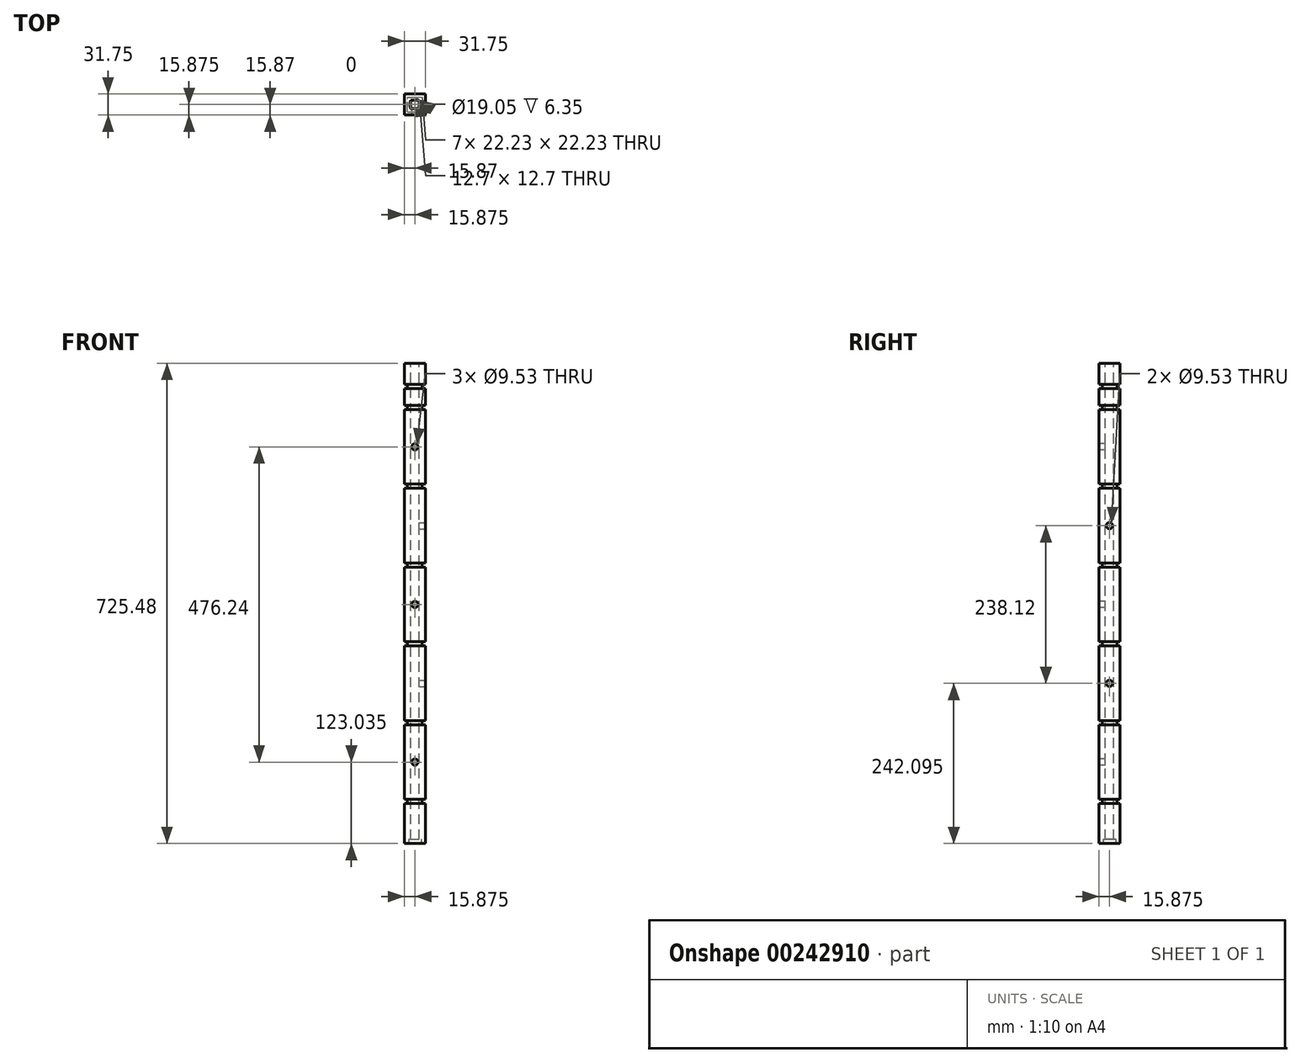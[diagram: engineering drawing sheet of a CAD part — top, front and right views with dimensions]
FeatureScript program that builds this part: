
annotation { "Feature Type Name" : "Feature", "Feature Type Description" : "" }
export const myFeature = defineFeature(function(context is Context, id is Id, definition is map)
    precondition{}
    {
        {
            var Q0;
            Q0=qCreatedBy(makeId("Top.planeOp"),FACE);
            var sketch = newSketch(context, id + "F0", { "sketchPlane" : qUnion([Q0])});
            skLineSegment(sketch, "E0", {"start": v(0, 0) * mm, "end": v(0, 31.75) * mm});
            skLineSegment(sketch, "E1", {"start": v(0, 31.75) * mm, "end": v(31.75, 31.75) * mm});
            skLineSegment(sketch, "E2", {"start": v(31.75, 31.75) * mm, "end": v(31.75, 0) * mm});
            skLineSegment(sketch, "E3", {"start": v(31.75, 0) * mm, "end": v(0, 0) * mm});
            skSolve(sketch);
        }
        {
            var Q0;
            Q0=makeQuery(id+"F0.imprint","IMPRINT",FACE,{"disambiguationData":[TD([[makeQuery(id+"F0.imprint","IMPRINT",EDGE,{"derivedFrom":sQuery(id+"F0.wireOp",EDGE,"E0")}),-1.0]])]});
            extrude(context, id + "F1", {"entities" : qUnion([Q0]), "depth" : 60.33 * mm});
        }
        {
            var Q0;
            Q0=makeQuery(id+"F1.opExtrude","CAP_FACE",FACE,{"disambiguationData":[OSD([sQuery(id+"F0.wireOp",EDGE,"E0"),sQuery(id+"F0.wireOp",EDGE,"E1"),sQuery(id+"F0.wireOp",EDGE,"E2"),sQuery(id+"F0.wireOp",EDGE,"E3")])],"isStart":false});
            var sketch = newSketch(context, id + "F2", { "sketchPlane" : qUnion([Q0])});
            skLineSegment(sketch, "E4", {"start": v(4.76, 4.76) * mm, "end": v(4.76, 26.99) * mm});
            skLineSegment(sketch, "E5", {"start": v(4.76, 26.99) * mm, "end": v(26.99, 26.99) * mm});
            skLineSegment(sketch, "E6", {"start": v(26.99, 26.99) * mm, "end": v(26.99, 4.76) * mm});
            skLineSegment(sketch, "E7", {"start": v(26.99, 4.76) * mm, "end": v(4.76, 4.76) * mm});
            skSolve(sketch);
        }
        {
            var Q0;
            Q0=makeQuery(id+"F2.imprint","IMPRINT",FACE,{"disambiguationData":[TD([[makeQuery(id+"F2.imprint","IMPRINT",EDGE,{"derivedFrom":sQuery(id+"F2.wireOp",EDGE,"E4")}),-1.0]])]});
            extrude(context, id + "F3", {"entities" : qUnion([Q0]), "operationType" : NewBodyOperationType.ADD, "depth" : 6.35 * mm});
        }
        {
            var Q0;
            Q0=makeQuery(id+"F3.opExtrude","CAP_FACE",FACE,{"disambiguationData":[OSD([sQuery(id+"F2.wireOp",EDGE,"E4"),sQuery(id+"F2.wireOp",EDGE,"E5"),sQuery(id+"F2.wireOp",EDGE,"E6"),sQuery(id+"F2.wireOp",EDGE,"E7")])],"isStart":false});
            var sketch = newSketch(context, id + "F4", { "sketchPlane" : qUnion([Q0])});
            skLineSegment(sketch, "E8.bottom", {"start": v(0, 0) * mm, "end": v(31.75, 0) * mm});
            skLineSegment(sketch, "E8.top", {"start": v(0, 31.75) * mm, "end": v(31.75, 31.75) * mm});
            skLineSegment(sketch, "E8.left", {"start": v(0, 0) * mm, "end": v(0, 31.75) * mm});
            skLineSegment(sketch, "E8.right", {"start": v(31.75, 0) * mm, "end": v(31.75, 31.75) * mm});
            skSolve(sketch);
        }
        {
            var Q0;
            Q0 = qSketchRegion(id + "F4", true);
            extrude(context, id + "F5", {"entities" : qUnion([Q0]), "operationType" : NewBodyOperationType.ADD, "depth" : 112.7 * mm});
        }
        {
            var Q0;
            Q0=makeQuery(id+"F5.opExtrude","CAP_FACE",FACE,{"disambiguationData":[OSD([sQuery(id+"F4.wireOp",EDGE,"E8.bottom"),sQuery(id+"F4.wireOp",EDGE,"E8.top"),sQuery(id+"F4.wireOp",EDGE,"E8.left"),sQuery(id+"F4.wireOp",EDGE,"E8.right")])],"isStart":false});
            var sketch = newSketch(context, id + "F6", { "sketchPlane" : qUnion([Q0])});
            skLineSegment(sketch, "E9.bottom", {"start": v(0, 0) * mm, "end": v(4.76, 0) * mm});
            skLineSegment(sketch, "E9.top", {"start": v(0, 4.76) * mm, "end": v(4.76, 4.76) * mm});
            skLineSegment(sketch, "E9.left", {"start": v(0, 0) * mm, "end": v(0, 4.76) * mm});
            skLineSegment(sketch, "E9.right", {"start": v(4.76, 0) * mm, "end": v(4.76, 4.76) * mm});
            skLineSegment(sketch, "E10.bottom", {"start": v(4.76, 4.76) * mm, "end": v(26.99, 4.76) * mm});
            skLineSegment(sketch, "E10.top", {"start": v(4.76, 26.99) * mm, "end": v(26.99, 26.99) * mm});
            skLineSegment(sketch, "E10.left", {"start": v(4.76, 4.76) * mm, "end": v(4.76, 26.99) * mm});
            skLineSegment(sketch, "E10.right", {"start": v(26.99, 4.76) * mm, "end": v(26.99, 26.99) * mm});
            skSolve(sketch);
        }
        {
            var Q0;
            Q0=makeQuery(id+"F6.imprint","IMPRINT",FACE,{"disambiguationData":[TD([[makeQuery(id+"F6.imprint","IMPRINT",EDGE,{"derivedFrom":sQuery(id+"F6.wireOp",EDGE,"E10.bottom")}),1.0]])]});
            extrude(context, id + "F7", {"entities" : qUnion([Q0]), "operationType" : NewBodyOperationType.ADD, "depth" : 6.35 * mm});
        }
        {
            var Q0;
            Q0=makeQuery(id+"F7.opExtrude","CAP_FACE",FACE,{"disambiguationData":[OSD([sQuery(id+"F6.wireOp",EDGE,"E10.bottom"),sQuery(id+"F6.wireOp",EDGE,"E10.top"),sQuery(id+"F6.wireOp",EDGE,"E10.left"),sQuery(id+"F6.wireOp",EDGE,"E10.right")])],"isStart":false});
            var sketch = newSketch(context, id + "F8", { "sketchPlane" : qUnion([Q0])});
            skLineSegment(sketch, "E11.bottom", {"start": v(0, 0) * mm, "end": v(31.75, 0) * mm});
            skLineSegment(sketch, "E11.top", {"start": v(0, 31.75) * mm, "end": v(31.75, 31.75) * mm});
            skLineSegment(sketch, "E11.left", {"start": v(0, 0) * mm, "end": v(0, 31.75) * mm});
            skLineSegment(sketch, "E11.right", {"start": v(31.75, 0) * mm, "end": v(31.75, 31.75) * mm});
            skSolve(sketch);
        }
        {
            var Q0;
            Q0=makeQuery(id+"F8.imprint","IMPRINT",FACE,{"disambiguationData":[TD([[makeQuery(id+"F8.imprint","IMPRINT",EDGE,{"derivedFrom":sQuery(id+"F8.wireOp",EDGE,"E11.bottom")}),1.0]])]});
            var Q1;
            Q1=makeQuery(id+"F8.imprint","IMPRINT",FACE,{"disambiguationData":[TD([[makeQuery(id+"F8.imprint","IMPRINT",EDGE,{"derivedFrom":makeQuery(id+"F7.opExtrude","CAP_EDGE",EDGE,{"disambiguationData":[OSD([sQuery(id+"F6.wireOp",EDGE,"E10.bottom")])],"isStart":false})}),1.0]])]});
            extrude(context, id + "F9", {"entities" : qUnion([Q0, Q1]), "operationType" : NewBodyOperationType.ADD, "depth" : 112.7 * mm});
        }
        {
            var Q0;
            Q0=makeQuery(id+"F9.opExtrude","CAP_FACE",FACE,{"disambiguationData":[OSD([sQuery(id+"F8.wireOp",EDGE,"E11.bottom"),sQuery(id+"F8.wireOp",EDGE,"E11.top"),sQuery(id+"F8.wireOp",EDGE,"E11.left"),sQuery(id+"F8.wireOp",EDGE,"E11.right")])],"isStart":false});
            var sketch = newSketch(context, id + "F10", { "sketchPlane" : qUnion([Q0])});
            skLineSegment(sketch, "E12.bottom", {"start": v(0, 0) * mm, "end": v(4.76, 0) * mm});
            skLineSegment(sketch, "E12.top", {"start": v(0, 4.76) * mm, "end": v(4.76, 4.76) * mm});
            skLineSegment(sketch, "E12.left", {"start": v(0, 0) * mm, "end": v(0, 4.76) * mm});
            skLineSegment(sketch, "E12.right", {"start": v(4.76, 0) * mm, "end": v(4.76, 4.76) * mm});
            skLineSegment(sketch, "E13.bottom", {"start": v(4.76, 4.76) * mm, "end": v(27, 4.76) * mm});
            skLineSegment(sketch, "E13.top", {"start": v(4.76, 26.99) * mm, "end": v(26.99, 26.99) * mm});
            skLineSegment(sketch, "E13.left", {"start": v(4.76, 4.76) * mm, "end": v(4.76, 26.99) * mm});
            skLineSegment(sketch, "E13.right", {"start": v(27, 4.76) * mm, "end": v(26.99, 26.99) * mm});
            skLineSegment(sketch, "E14.bottom", {"start": v(26.99, 26.99) * mm, "end": v(31.75, 26.99) * mm});
            skLineSegment(sketch, "E14.top", {"start": v(26.99, 31.75) * mm, "end": v(31.75, 31.75) * mm});
            skLineSegment(sketch, "E14.left", {"start": v(26.99, 26.99) * mm, "end": v(26.99, 31.75) * mm});
            skLineSegment(sketch, "E14.right", {"start": v(31.75, 26.99) * mm, "end": v(31.75, 31.75) * mm});
            skSolve(sketch);
        }
        {
            var Q0;
            Q0=makeQuery(id+"F10.imprint","IMPRINT",FACE,{"disambiguationData":[TD([[makeQuery(id+"F10.imprint","IMPRINT",EDGE,{"derivedFrom":sQuery(id+"F10.wireOp",EDGE,"E13.bottom")}),1.0]])]});
            extrude(context, id + "F11", {"entities" : qUnion([Q0]), "operationType" : NewBodyOperationType.ADD, "depth" : 6.35 * mm});
        }
        {
            var Q0;
            Q0=makeQuery(id+"F11.opExtrude","CAP_FACE",FACE,{"disambiguationData":[OSD([sQuery(id+"F10.wireOp",EDGE,"E13.bottom"),sQuery(id+"F10.wireOp",EDGE,"E13.top"),sQuery(id+"F10.wireOp",EDGE,"E13.left"),sQuery(id+"F10.wireOp",EDGE,"E13.right")])],"isStart":false});
            var sketch = newSketch(context, id + "F12", { "sketchPlane" : qUnion([Q0])});
            skLineSegment(sketch, "E15.bottom", {"start": v(0, 0) * mm, "end": v(31.75, 0) * mm});
            skLineSegment(sketch, "E15.top", {"start": v(0, 31.75) * mm, "end": v(31.75, 31.75) * mm});
            skLineSegment(sketch, "E15.left", {"start": v(0, 0) * mm, "end": v(0, 31.75) * mm});
            skLineSegment(sketch, "E15.right", {"start": v(31.75, 0) * mm, "end": v(31.75, 31.75) * mm});
            skSolve(sketch);
        }
        {
            var Q0;
            Q0=makeQuery(id+"F12.imprint","IMPRINT",FACE,{"disambiguationData":[TD([[makeQuery(id+"F12.imprint","IMPRINT",EDGE,{"derivedFrom":makeQuery(id+"F11.opExtrude","CAP_EDGE",EDGE,{"disambiguationData":[OSD([sQuery(id+"F10.wireOp",EDGE,"E13.bottom")])],"isStart":false})}),1.0]])]});
            var Q1;
            Q1=makeQuery(id+"F12.imprint","IMPRINT",FACE,{"disambiguationData":[TD([[makeQuery(id+"F12.imprint","IMPRINT",EDGE,{"derivedFrom":sQuery(id+"F12.wireOp",EDGE,"E15.bottom")}),1.0]])]});
            extrude(context, id + "F13", {"entities" : qUnion([Q0, Q1]), "operationType" : NewBodyOperationType.ADD, "depth" : 112.7 * mm});
        }
        {
            var Q0;
            Q0=makeQuery(id+"F13.opExtrude","CAP_FACE",FACE,{"disambiguationData":[OSD([sQuery(id+"F12.wireOp",EDGE,"E15.bottom"),sQuery(id+"F12.wireOp",EDGE,"E15.top"),sQuery(id+"F12.wireOp",EDGE,"E15.left"),sQuery(id+"F12.wireOp",EDGE,"E15.right")])],"isStart":false});
            var sketch = newSketch(context, id + "F14", { "sketchPlane" : qUnion([Q0])});
            skLineSegment(sketch, "E16.bottom", {"start": v(0, 0) * mm, "end": v(4.76, 0) * mm});
            skLineSegment(sketch, "E16.top", {"start": v(0, 4.76) * mm, "end": v(4.76, 4.76) * mm});
            skLineSegment(sketch, "E16.left", {"start": v(0, 0) * mm, "end": v(0, 4.76) * mm});
            skLineSegment(sketch, "E16.right", {"start": v(4.76, 0) * mm, "end": v(4.76, 4.76) * mm});
            skLineSegment(sketch, "E17.bottom", {"start": v(4.76, 4.76) * mm, "end": v(27, 4.76) * mm});
            skLineSegment(sketch, "E17.top", {"start": v(4.76, 26.99) * mm, "end": v(26.99, 26.99) * mm});
            skLineSegment(sketch, "E17.left", {"start": v(4.76, 4.76) * mm, "end": v(4.76, 26.99) * mm});
            skLineSegment(sketch, "E17.right", {"start": v(27, 4.76) * mm, "end": v(26.99, 26.99) * mm});
            skLineSegment(sketch, "E18.bottom", {"start": v(26.99, 26.99) * mm, "end": v(31.75, 26.99) * mm});
            skLineSegment(sketch, "E18.top", {"start": v(26.99, 31.75) * mm, "end": v(31.75, 31.75) * mm});
            skLineSegment(sketch, "E18.left", {"start": v(26.99, 26.99) * mm, "end": v(26.99, 31.75) * mm});
            skLineSegment(sketch, "E18.right", {"start": v(31.75, 26.99) * mm, "end": v(31.75, 31.75) * mm});
            skSolve(sketch);
        }
        {
            var Q0;
            Q0=makeQuery(id+"F14.imprint","IMPRINT",FACE,{"disambiguationData":[TD([[makeQuery(id+"F14.imprint","IMPRINT",EDGE,{"derivedFrom":sQuery(id+"F14.wireOp",EDGE,"E17.bottom")}),1.0]])]});
            extrude(context, id + "F15", {"entities" : qUnion([Q0]), "operationType" : NewBodyOperationType.ADD, "depth" : 6.35 * mm});
        }
        {
            var Q0;
            Q0=makeQuery(id+"F15.opExtrude","CAP_FACE",FACE,{"disambiguationData":[OSD([sQuery(id+"F14.wireOp",EDGE,"E17.bottom"),sQuery(id+"F14.wireOp",EDGE,"E17.top"),sQuery(id+"F14.wireOp",EDGE,"E17.left"),sQuery(id+"F14.wireOp",EDGE,"E17.right")])],"isStart":false});
            var sketch = newSketch(context, id + "F16", { "sketchPlane" : qUnion([Q0])});
            skLineSegment(sketch, "E19.bottom", {"start": v(0, 0) * mm, "end": v(31.75, 0) * mm});
            skLineSegment(sketch, "E19.top", {"start": v(0, 31.75) * mm, "end": v(31.75, 31.75) * mm});
            skLineSegment(sketch, "E19.left", {"start": v(0, 0) * mm, "end": v(0, 31.75) * mm});
            skLineSegment(sketch, "E19.right", {"start": v(31.75, 0) * mm, "end": v(31.75, 31.75) * mm});
            skSolve(sketch);
        }
        {
            var Q0;
            Q0 = qSketchRegion(id + "F16", true);
            extrude(context, id + "F17", {"entities" : qUnion([Q0]), "operationType" : NewBodyOperationType.ADD, "depth" : 112.7 * mm});
        }
        {
            var Q0;
            Q0=makeQuery(id+"F17.opExtrude","CAP_FACE",FACE,{"disambiguationData":[OSD([sQuery(id+"F16.wireOp",EDGE,"E19.bottom"),sQuery(id+"F16.wireOp",EDGE,"E19.top"),sQuery(id+"F16.wireOp",EDGE,"E19.left"),sQuery(id+"F16.wireOp",EDGE,"E19.right")])],"isStart":false});
            var sketch = newSketch(context, id + "F18", { "sketchPlane" : qUnion([Q0])});
            skLineSegment(sketch, "E20.bottom", {"start": v(0, 0) * mm, "end": v(4.76, 0) * mm});
            skLineSegment(sketch, "E20.top", {"start": v(0, 4.76) * mm, "end": v(4.76, 4.76) * mm});
            skLineSegment(sketch, "E20.left", {"start": v(0, 0) * mm, "end": v(0, 4.76) * mm});
            skLineSegment(sketch, "E20.right", {"start": v(4.76, 0) * mm, "end": v(4.76, 4.76) * mm});
            skLineSegment(sketch, "E21.bottom", {"start": v(4.76, 4.76) * mm, "end": v(27, 4.76) * mm});
            skLineSegment(sketch, "E21.top", {"start": v(4.76, 26.99) * mm, "end": v(26.99, 26.99) * mm});
            skLineSegment(sketch, "E21.left", {"start": v(4.76, 4.76) * mm, "end": v(4.76, 26.99) * mm});
            skLineSegment(sketch, "E21.right", {"start": v(27, 4.76) * mm, "end": v(26.99, 26.99) * mm});
            skLineSegment(sketch, "E22.bottom", {"start": v(26.99, 26.99) * mm, "end": v(31.75, 26.99) * mm});
            skLineSegment(sketch, "E22.top", {"start": v(26.99, 31.75) * mm, "end": v(31.75, 31.75) * mm});
            skLineSegment(sketch, "E22.left", {"start": v(26.99, 26.99) * mm, "end": v(26.99, 31.75) * mm});
            skLineSegment(sketch, "E22.right", {"start": v(31.75, 26.99) * mm, "end": v(31.75, 31.75) * mm});
            skSolve(sketch);
        }
        {
            var Q0;
            Q0=makeQuery(id+"F18.imprint","IMPRINT",FACE,{"disambiguationData":[TD([[makeQuery(id+"F18.imprint","IMPRINT",EDGE,{"derivedFrom":sQuery(id+"F18.wireOp",EDGE,"E21.bottom")}),1.0]])]});
            extrude(context, id + "F19", {"entities" : qUnion([Q0]), "operationType" : NewBodyOperationType.ADD, "depth" : 6.35 * mm});
        }
        {
            var Q0;
            Q0=makeQuery(id+"F19.opExtrude","CAP_FACE",FACE,{"disambiguationData":[OSD([sQuery(id+"F18.wireOp",EDGE,"E21.bottom"),sQuery(id+"F18.wireOp",EDGE,"E21.top"),sQuery(id+"F18.wireOp",EDGE,"E21.left"),sQuery(id+"F18.wireOp",EDGE,"E21.right")])],"isStart":false});
            var sketch = newSketch(context, id + "F20", { "sketchPlane" : qUnion([Q0])});
            skLineSegment(sketch, "E23.bottom", {"start": v(0, 0) * mm, "end": v(31.75, 0) * mm});
            skLineSegment(sketch, "E23.top", {"start": v(0, 31.75) * mm, "end": v(31.75, 31.75) * mm});
            skLineSegment(sketch, "E23.left", {"start": v(0, 0) * mm, "end": v(0, 31.75) * mm});
            skLineSegment(sketch, "E23.right", {"start": v(31.75, 0) * mm, "end": v(31.75, 31.75) * mm});
            skSolve(sketch);
        }
        {
            var Q0;
            Q0=makeQuery(id+"F20.imprint","IMPRINT",FACE,{"disambiguationData":[TD([[makeQuery(id+"F20.imprint","IMPRINT",EDGE,{"derivedFrom":sQuery(id+"F20.wireOp",EDGE,"E23.bottom")}),1.0]])]});
            var Q1;
            Q1=makeQuery(id+"F20.imprint","IMPRINT",FACE,{"disambiguationData":[TD([[makeQuery(id+"F20.imprint","IMPRINT",EDGE,{"derivedFrom":makeQuery(id+"F19.opExtrude","CAP_EDGE",EDGE,{"disambiguationData":[OSD([sQuery(id+"F18.wireOp",EDGE,"E21.bottom")])],"isStart":false})}),1.0]])]});
            extrude(context, id + "F21", {"entities" : qUnion([Q0, Q1]), "operationType" : NewBodyOperationType.ADD, "depth" : 112.7 * mm});
        }
        {
            var Q0;
            Q0=makeQuery(id+"F21.opExtrude","CAP_FACE",FACE,{"disambiguationData":[OSD([sQuery(id+"F20.wireOp",EDGE,"E23.bottom"),sQuery(id+"F20.wireOp",EDGE,"E23.top"),sQuery(id+"F20.wireOp",EDGE,"E23.left"),sQuery(id+"F20.wireOp",EDGE,"E23.right")])],"isStart":false});
            var sketch = newSketch(context, id + "F22", { "sketchPlane" : qUnion([Q0])});
            skLineSegment(sketch, "E24.bottom", {"start": v(0, 0) * mm, "end": v(4.76, 0) * mm});
            skLineSegment(sketch, "E24.top", {"start": v(0, 4.76) * mm, "end": v(4.76, 4.76) * mm});
            skLineSegment(sketch, "E24.left", {"start": v(0, 0) * mm, "end": v(0, 4.76) * mm});
            skLineSegment(sketch, "E24.right", {"start": v(4.76, 0) * mm, "end": v(4.76, 4.76) * mm});
            skLineSegment(sketch, "E25.bottom", {"start": v(4.76, 4.76) * mm, "end": v(27, 4.76) * mm});
            skLineSegment(sketch, "E25.top", {"start": v(4.76, 26.99) * mm, "end": v(26.99, 26.99) * mm});
            skLineSegment(sketch, "E25.left", {"start": v(4.76, 4.76) * mm, "end": v(4.76, 26.99) * mm});
            skLineSegment(sketch, "E25.right", {"start": v(27, 4.76) * mm, "end": v(26.99, 26.99) * mm});
            skLineSegment(sketch, "E26.bottom", {"start": v(26.99, 26.99) * mm, "end": v(31.75, 26.99) * mm});
            skLineSegment(sketch, "E26.top", {"start": v(26.99, 31.75) * mm, "end": v(31.75, 31.75) * mm});
            skLineSegment(sketch, "E26.left", {"start": v(26.99, 26.99) * mm, "end": v(26.99, 31.75) * mm});
            skLineSegment(sketch, "E26.right", {"start": v(31.75, 26.99) * mm, "end": v(31.75, 31.75) * mm});
            skSolve(sketch);
        }
        {
            var Q0;
            Q0=makeQuery(id+"F22.imprint","IMPRINT",FACE,{"disambiguationData":[TD([[makeQuery(id+"F22.imprint","IMPRINT",EDGE,{"derivedFrom":sQuery(id+"F22.wireOp",EDGE,"E25.bottom")}),1.0]])]});
            extrude(context, id + "F23", {"entities" : qUnion([Q0]), "operationType" : NewBodyOperationType.ADD, "depth" : 6.35 * mm});
        }
        {
            var Q0;
            Q0=makeQuery(id+"F23.opExtrude","CAP_FACE",FACE,{"disambiguationData":[OSD([sQuery(id+"F22.wireOp",EDGE,"E25.bottom"),sQuery(id+"F22.wireOp",EDGE,"E25.top"),sQuery(id+"F22.wireOp",EDGE,"E25.left"),sQuery(id+"F22.wireOp",EDGE,"E25.right")])],"isStart":false});
            var sketch = newSketch(context, id + "F24", { "sketchPlane" : qUnion([Q0])});
            skLineSegment(sketch, "E27.bottom", {"start": v(0, 0) * mm, "end": v(31.75, 0) * mm});
            skLineSegment(sketch, "E27.top", {"start": v(0, 31.75) * mm, "end": v(31.75, 31.75) * mm});
            skLineSegment(sketch, "E27.left", {"start": v(0, 0) * mm, "end": v(0, 31.75) * mm});
            skLineSegment(sketch, "E27.right", {"start": v(31.75, 0) * mm, "end": v(31.75, 31.75) * mm});
            skSolve(sketch);
        }
        {
            var Q0;
            Q0=makeQuery(id+"F24.imprint","IMPRINT",FACE,{"disambiguationData":[TD([[makeQuery(id+"F24.imprint","IMPRINT",EDGE,{"derivedFrom":sQuery(id+"F24.wireOp",EDGE,"E27.bottom")}),1.0]])]});
            var Q1;
            Q1=makeQuery(id+"F24.imprint","IMPRINT",FACE,{"disambiguationData":[TD([[makeQuery(id+"F24.imprint","IMPRINT",EDGE,{"derivedFrom":makeQuery(id+"F23.opExtrude","CAP_EDGE",EDGE,{"disambiguationData":[OSD([sQuery(id+"F22.wireOp",EDGE,"E25.bottom")])],"isStart":false})}),1.0]])]});
            extrude(context, id + "F25", {"entities" : qUnion([Q0, Q1]), "operationType" : NewBodyOperationType.ADD, "depth" : 25.4 * mm});
        }
        {
            var Q0;
            Q0=makeQuery(id+"F25.opExtrude","CAP_FACE",FACE,{"disambiguationData":[OSD([sQuery(id+"F24.wireOp",EDGE,"E27.bottom"),sQuery(id+"F24.wireOp",EDGE,"E27.top"),sQuery(id+"F24.wireOp",EDGE,"E27.left"),sQuery(id+"F24.wireOp",EDGE,"E27.right")])],"isStart":false});
            var sketch = newSketch(context, id + "F26", { "sketchPlane" : qUnion([Q0])});
            skLineSegment(sketch, "E28.bottom", {"start": v(0, 0) * mm, "end": v(4.76, 0) * mm});
            skLineSegment(sketch, "E28.top", {"start": v(0, 4.76) * mm, "end": v(4.76, 4.76) * mm});
            skLineSegment(sketch, "E28.left", {"start": v(0, 0) * mm, "end": v(0, 4.76) * mm});
            skLineSegment(sketch, "E28.right", {"start": v(4.76, 0) * mm, "end": v(4.76, 4.76) * mm});
            skLineSegment(sketch, "E29.bottom", {"start": v(4.76, 4.76) * mm, "end": v(27, 4.76) * mm});
            skLineSegment(sketch, "E29.top", {"start": v(4.76, 26.99) * mm, "end": v(26.99, 26.99) * mm});
            skLineSegment(sketch, "E29.left", {"start": v(4.76, 4.76) * mm, "end": v(4.76, 26.99) * mm});
            skLineSegment(sketch, "E29.right", {"start": v(27, 4.76) * mm, "end": v(26.99, 26.99) * mm});
            skLineSegment(sketch, "E30.bottom", {"start": v(26.99, 26.99) * mm, "end": v(31.75, 26.99) * mm});
            skLineSegment(sketch, "E30.top", {"start": v(26.99, 31.75) * mm, "end": v(31.75, 31.75) * mm});
            skLineSegment(sketch, "E30.left", {"start": v(26.99, 26.99) * mm, "end": v(26.99, 31.75) * mm});
            skLineSegment(sketch, "E30.right", {"start": v(31.75, 26.99) * mm, "end": v(31.75, 31.75) * mm});
            skSolve(sketch);
        }
        {
            var Q0;
            Q0=makeQuery(id+"F26.imprint","IMPRINT",FACE,{"disambiguationData":[TD([[makeQuery(id+"F26.imprint","IMPRINT",EDGE,{"derivedFrom":sQuery(id+"F26.wireOp",EDGE,"E29.bottom")}),1.0]])]});
            extrude(context, id + "F27", {"entities" : qUnion([Q0]), "operationType" : NewBodyOperationType.ADD, "depth" : 6.35 * mm});
        }
        {
            var Q0;
            Q0=makeQuery(id+"F27.opExtrude","CAP_FACE",FACE,{"disambiguationData":[OSD([sQuery(id+"F26.wireOp",EDGE,"E29.bottom"),sQuery(id+"F26.wireOp",EDGE,"E29.top"),sQuery(id+"F26.wireOp",EDGE,"E29.left"),sQuery(id+"F26.wireOp",EDGE,"E29.right")])],"isStart":false});
            var sketch = newSketch(context, id + "F28", { "sketchPlane" : qUnion([Q0])});
            skLineSegment(sketch, "E31.bottom", {"start": v(0, 0) * mm, "end": v(31.75, 0) * mm});
            skLineSegment(sketch, "E31.top", {"start": v(0, 31.75) * mm, "end": v(31.75, 31.75) * mm});
            skLineSegment(sketch, "E31.left", {"start": v(0, 0) * mm, "end": v(0, 31.75) * mm});
            skLineSegment(sketch, "E31.right", {"start": v(31.75, 0) * mm, "end": v(31.75, 31.75) * mm});
            skSolve(sketch);
        }
        {
            var Q0;
            Q0=makeQuery(id+"F28.imprint","IMPRINT",FACE,{"disambiguationData":[TD([[makeQuery(id+"F28.imprint","IMPRINT",EDGE,{"derivedFrom":sQuery(id+"F28.wireOp",EDGE,"E31.bottom")}),1.0]])]});
            var Q1;
            Q1=makeQuery(id+"F28.imprint","IMPRINT",FACE,{"disambiguationData":[TD([[makeQuery(id+"F28.imprint","IMPRINT",EDGE,{"derivedFrom":makeQuery(id+"F27.opExtrude","CAP_EDGE",EDGE,{"disambiguationData":[OSD([sQuery(id+"F26.wireOp",EDGE,"E29.bottom")])],"isStart":false})}),1.0]])]});
            extrude(context, id + "F29", {"entities" : qUnion([Q0, Q1]), "operationType" : NewBodyOperationType.ADD, "depth" : 31.75 * mm});
        }
        {
            var Q0;
            Q0=makeQuery(id+"F1.opExtrude","CAP_FACE",FACE,{"disambiguationData":[OSD([sQuery(id+"F0.wireOp",EDGE,"E0"),sQuery(id+"F0.wireOp",EDGE,"E1"),sQuery(id+"F0.wireOp",EDGE,"E2"),sQuery(id+"F0.wireOp",EDGE,"E3")])],"isStart":true});
            var sketch = newSketch(context, id + "F30", { "sketchPlane" : qUnion([Q0])});
            skLineSegment(sketch, "E32.bottom", {"start": v(0, -31.75) * mm, "end": v(15.88, -31.75) * mm});
            skLineSegment(sketch, "E32.top", {"start": v(0, -15.87) * mm, "end": v(15.88, -15.87) * mm});
            skLineSegment(sketch, "E32.left", {"start": v(0, -31.75) * mm, "end": v(0, -15.87) * mm});
            skLineSegment(sketch, "E32.right", {"start": v(15.88, -31.75) * mm, "end": v(15.88, -15.87) * mm});
            skLineSegment(sketch, "E33", {"start": v(0, -31.75) * mm, "end": v(31.75, -31.75) * mm});
            skCircle(sketch, "E34", {"center": v(15.88, -15.87) * mm, "radius": 15.88 * mm});
            skCircle(sketch, "E35", {"center": v(15.88, -15.87) * mm, "radius": 9.53 * mm});
            skSolve(sketch);
        }
        {
            var Q0;
            Q0=makeQuery(id+"F5.opExtrude","SWEPT_FACE",FACE,{"disambiguationData":[OSD([sQuery(id+"F4.wireOp",EDGE,"E8.bottom")])]});
            var sketch = newSketch(context, id + "F31", { "sketchPlane" : qUnion([Q0])});
            skLineSegment(sketch, "E36.bottom", {"start": v(31.75, 123.04) * mm, "end": v(15.88, 123.04) * mm});
            skLineSegment(sketch, "E36.top", {"start": v(31.75, 66.68) * mm, "end": v(15.88, 66.68) * mm});
            skLineSegment(sketch, "E36.left", {"start": v(31.75, 123.04) * mm, "end": v(31.75, 66.68) * mm});
            skLineSegment(sketch, "E36.right", {"start": v(15.88, 123.04) * mm, "end": v(15.88, 66.68) * mm});
            skCircle(sketch, "E37", {"center": v(15.88, 123.04) * mm, "radius": 4.77 * mm});
            skSolve(sketch);
        }
        {
            var Q0;
            {var subQ0=sQuery(id+"F31.wireOp",EDGE,"E36.right");var subQ1=sQuery(id+"F31.wireOp",EDGE,"E36.bottom");var subQ2=makeQuery(id+"F31.imprint","INTERSECT",VERTEX,{"derivedFrom":[subQ1,subQ0]});Q0=makeQuery(id+"F31.imprint","IMPRINT",FACE,{"disambiguationData":[TD([[makeQuery(id+"F31.imprint","IMPRINT",EDGE,{"disambiguationData":[TD([[subQ2,1.0]])],"derivedFrom":subQ1}),-1.0]])]});}
            var Q1;
            {var subQ0=sQuery(id+"F31.wireOp",EDGE,"E36.right");var subQ1=sQuery(id+"F31.wireOp",EDGE,"E36.bottom");var subQ2=makeQuery(id+"F31.imprint","INTERSECT",VERTEX,{"derivedFrom":[subQ1,subQ0]});Q1=makeQuery(id+"F31.imprint","IMPRINT",FACE,{"disambiguationData":[TD([[makeQuery(id+"F31.imprint","IMPRINT",EDGE,{"disambiguationData":[TD([[subQ2,1.0]])],"derivedFrom":subQ1}),1.0]])]});}
            extrude(context, id + "F32", {"entities" : qUnion([Q0, Q1]), "operationType" : NewBodyOperationType.REMOVE, "oppositeDirection" : true, "depth" : 12.7 * mm});
        }
        {
            var Q0;
            Q0=makeQuery(id+"F9.opExtrude","SWEPT_FACE",FACE,{"disambiguationData":[OSD([sQuery(id+"F8.wireOp",EDGE,"E11.right")])]});
            var sketch = newSketch(context, id + "F33", { "sketchPlane" : qUnion([Q0])});
            skLineSegment(sketch, "E38.bottom", {"start": v(31.75, 242.1) * mm, "end": v(15.88, 242.1) * mm});
            skLineSegment(sketch, "E38.top", {"start": v(31.75, 185.74) * mm, "end": v(15.88, 185.74) * mm});
            skLineSegment(sketch, "E38.left", {"start": v(31.75, 242.1) * mm, "end": v(31.75, 185.74) * mm});
            skLineSegment(sketch, "E38.right", {"start": v(15.88, 242.1) * mm, "end": v(15.88, 185.74) * mm});
            skCircle(sketch, "E39", {"center": v(15.88, 242.1) * mm, "radius": 4.77 * mm});
            skSolve(sketch);
        }
        {
            var Q0;
            {var subQ0=sQuery(id+"F33.wireOp",EDGE,"E38.right");var subQ1=sQuery(id+"F33.wireOp",EDGE,"E38.bottom");var subQ2=makeQuery(id+"F33.imprint","INTERSECT",VERTEX,{"derivedFrom":[subQ1,subQ0]});Q0=makeQuery(id+"F33.imprint","IMPRINT",FACE,{"disambiguationData":[TD([[makeQuery(id+"F33.imprint","IMPRINT",EDGE,{"disambiguationData":[TD([[subQ2,1.0]])],"derivedFrom":subQ1}),-1.0]])]});}
            var Q1;
            {var subQ0=sQuery(id+"F33.wireOp",EDGE,"E38.right");var subQ1=sQuery(id+"F33.wireOp",EDGE,"E38.bottom");var subQ2=makeQuery(id+"F33.imprint","INTERSECT",VERTEX,{"derivedFrom":[subQ1,subQ0]});Q1=makeQuery(id+"F33.imprint","IMPRINT",FACE,{"disambiguationData":[TD([[makeQuery(id+"F33.imprint","IMPRINT",EDGE,{"disambiguationData":[TD([[subQ2,1.0]])],"derivedFrom":subQ1}),1.0]])]});}
            extrude(context, id + "F34", {"entities" : qUnion([Q0, Q1]), "operationType" : NewBodyOperationType.REMOVE, "oppositeDirection" : true, "depth" : 12.7 * mm});
        }
        {
            var Q0;
            Q0=makeQuery(id+"F13.opExtrude","SWEPT_FACE",FACE,{"disambiguationData":[OSD([sQuery(id+"F12.wireOp",EDGE,"E15.bottom")])]});
            var sketch = newSketch(context, id + "F35", { "sketchPlane" : qUnion([Q0])});
            skLineSegment(sketch, "E40.bottom", {"start": v(31.75, 361.16) * mm, "end": v(15.88, 361.16) * mm});
            skLineSegment(sketch, "E40.top", {"start": v(31.75, 304.8) * mm, "end": v(15.88, 304.8) * mm});
            skLineSegment(sketch, "E40.left", {"start": v(31.75, 361.16) * mm, "end": v(31.75, 304.8) * mm});
            skLineSegment(sketch, "E40.right", {"start": v(15.88, 361.16) * mm, "end": v(15.88, 304.8) * mm});
            skCircle(sketch, "E41", {"center": v(15.88, 361.16) * mm, "radius": 4.77 * mm});
            skSolve(sketch);
        }
        {
            var Q0;
            {var subQ0=sQuery(id+"F35.wireOp",EDGE,"E40.right");var subQ1=sQuery(id+"F35.wireOp",EDGE,"E40.bottom");var subQ2=makeQuery(id+"F35.imprint","INTERSECT",VERTEX,{"derivedFrom":[subQ1,subQ0]});Q0=makeQuery(id+"F35.imprint","IMPRINT",FACE,{"disambiguationData":[TD([[makeQuery(id+"F35.imprint","IMPRINT",EDGE,{"disambiguationData":[TD([[subQ2,1.0]])],"derivedFrom":subQ1}),-1.0]])]});}
            var Q1;
            {var subQ0=sQuery(id+"F35.wireOp",EDGE,"E40.right");var subQ1=sQuery(id+"F35.wireOp",EDGE,"E40.bottom");var subQ2=makeQuery(id+"F35.imprint","INTERSECT",VERTEX,{"derivedFrom":[subQ1,subQ0]});Q1=makeQuery(id+"F35.imprint","IMPRINT",FACE,{"disambiguationData":[TD([[makeQuery(id+"F35.imprint","IMPRINT",EDGE,{"disambiguationData":[TD([[subQ2,1.0]])],"derivedFrom":subQ1}),1.0]])]});}
            extrude(context, id + "F36", {"entities" : qUnion([Q0, Q1]), "operationType" : NewBodyOperationType.REMOVE, "oppositeDirection" : true, "depth" : 12.7 * mm});
        }
        {
            var Q0;
            Q0=makeQuery(id+"F17.opExtrude","SWEPT_FACE",FACE,{"disambiguationData":[OSD([sQuery(id+"F16.wireOp",EDGE,"E19.right")])]});
            var sketch = newSketch(context, id + "F37", { "sketchPlane" : qUnion([Q0])});
            skLineSegment(sketch, "E42.bottom", {"start": v(31.75, 480.21) * mm, "end": v(15.88, 480.21) * mm});
            skLineSegment(sketch, "E42.top", {"start": v(31.75, 423.86) * mm, "end": v(15.88, 423.86) * mm});
            skLineSegment(sketch, "E42.left", {"start": v(31.75, 480.21) * mm, "end": v(31.75, 423.86) * mm});
            skLineSegment(sketch, "E42.right", {"start": v(15.88, 480.21) * mm, "end": v(15.88, 423.86) * mm});
            skCircle(sketch, "E43", {"center": v(15.88, 480.21) * mm, "radius": 4.77 * mm});
            skSolve(sketch);
        }
        {
            var Q0;
            {var subQ0=sQuery(id+"F37.wireOp",EDGE,"E42.right");var subQ1=sQuery(id+"F37.wireOp",EDGE,"E42.bottom");var subQ2=makeQuery(id+"F37.imprint","INTERSECT",VERTEX,{"derivedFrom":[subQ1,subQ0]});Q0=makeQuery(id+"F37.imprint","IMPRINT",FACE,{"disambiguationData":[TD([[makeQuery(id+"F37.imprint","IMPRINT",EDGE,{"disambiguationData":[TD([[subQ2,1.0]])],"derivedFrom":subQ1}),-1.0]])]});}
            var Q1;
            {var subQ0=sQuery(id+"F37.wireOp",EDGE,"E42.right");var subQ1=sQuery(id+"F37.wireOp",EDGE,"E42.bottom");var subQ2=makeQuery(id+"F37.imprint","INTERSECT",VERTEX,{"derivedFrom":[subQ1,subQ0]});Q1=makeQuery(id+"F37.imprint","IMPRINT",FACE,{"disambiguationData":[TD([[makeQuery(id+"F37.imprint","IMPRINT",EDGE,{"disambiguationData":[TD([[subQ2,1.0]])],"derivedFrom":subQ1}),1.0]])]});}
            extrude(context, id + "F38", {"entities" : qUnion([Q0, Q1]), "operationType" : NewBodyOperationType.REMOVE, "oppositeDirection" : true, "depth" : 12.7 * mm});
        }
        {
            var Q0;
            Q0=makeQuery(id+"F21.opExtrude","SWEPT_FACE",FACE,{"disambiguationData":[OSD([sQuery(id+"F20.wireOp",EDGE,"E23.bottom")])]});
            var sketch = newSketch(context, id + "F39", { "sketchPlane" : qUnion([Q0])});
            skLineSegment(sketch, "E44.bottom", {"start": v(31.75, 599.27) * mm, "end": v(15.88, 599.27) * mm});
            skLineSegment(sketch, "E44.top", {"start": v(31.75, 542.92) * mm, "end": v(15.88, 542.92) * mm});
            skLineSegment(sketch, "E44.left", {"start": v(31.75, 599.27) * mm, "end": v(31.75, 542.92) * mm});
            skLineSegment(sketch, "E44.right", {"start": v(15.88, 599.27) * mm, "end": v(15.88, 542.92) * mm});
            skCircle(sketch, "E45", {"center": v(15.88, 599.27) * mm, "radius": 4.77 * mm});
            skSolve(sketch);
        }
        {
            var Q0;
            {var subQ0=sQuery(id+"F39.wireOp",EDGE,"E44.right");var subQ1=sQuery(id+"F39.wireOp",EDGE,"E44.bottom");var subQ2=makeQuery(id+"F39.imprint","INTERSECT",VERTEX,{"derivedFrom":[subQ1,subQ0]});Q0=makeQuery(id+"F39.imprint","IMPRINT",FACE,{"disambiguationData":[TD([[makeQuery(id+"F39.imprint","IMPRINT",EDGE,{"disambiguationData":[TD([[subQ2,1.0]])],"derivedFrom":subQ1}),-1.0]])]});}
            var Q1;
            {var subQ0=sQuery(id+"F39.wireOp",EDGE,"E44.right");var subQ1=sQuery(id+"F39.wireOp",EDGE,"E44.bottom");var subQ2=makeQuery(id+"F39.imprint","INTERSECT",VERTEX,{"derivedFrom":[subQ1,subQ0]});Q1=makeQuery(id+"F39.imprint","IMPRINT",FACE,{"disambiguationData":[TD([[makeQuery(id+"F39.imprint","IMPRINT",EDGE,{"disambiguationData":[TD([[subQ2,1.0]])],"derivedFrom":subQ1}),1.0]])]});}
            extrude(context, id + "F40", {"entities" : qUnion([Q0, Q1]), "operationType" : NewBodyOperationType.REMOVE, "oppositeDirection" : true, "depth" : 12.7 * mm});
        }
        {
            var Q0;
            Q0=makeQuery(id+"F29.opExtrude","CAP_FACE",FACE,{"disambiguationData":[OSD([sQuery(id+"F28.wireOp",EDGE,"E31.bottom"),sQuery(id+"F28.wireOp",EDGE,"E31.top"),sQuery(id+"F28.wireOp",EDGE,"E31.left"),sQuery(id+"F28.wireOp",EDGE,"E31.right")])],"isStart":false});
            var sketch = newSketch(context, id + "F41", { "sketchPlane" : qUnion([Q0])});
            skLineSegment(sketch, "E46.bottom", {"start": v(0, 0) * mm, "end": v(9.52, 0) * mm});
            skLineSegment(sketch, "E46.top", {"start": v(0, 9.52) * mm, "end": v(9.52, 9.52) * mm});
            skLineSegment(sketch, "E46.left", {"start": v(0, 0) * mm, "end": v(0, 9.52) * mm});
            skLineSegment(sketch, "E46.right", {"start": v(9.52, 0) * mm, "end": v(9.52, 9.52) * mm});
            skLineSegment(sketch, "E47.bottom", {"start": v(9.52, 9.52) * mm, "end": v(22.22, 9.52) * mm});
            skLineSegment(sketch, "E47.top", {"start": v(9.52, 22.22) * mm, "end": v(22.22, 22.22) * mm});
            skLineSegment(sketch, "E47.left", {"start": v(9.52, 9.52) * mm, "end": v(9.52, 22.22) * mm});
            skLineSegment(sketch, "E47.right", {"start": v(22.22, 9.52) * mm, "end": v(22.22, 22.22) * mm});
            skSolve(sketch);
        }
        {
            var Q0;
            Q0=makeQuery(id+"F41.imprint","IMPRINT",FACE,{"disambiguationData":[TD([[makeQuery(id+"F41.imprint","IMPRINT",EDGE,{"derivedFrom":sQuery(id+"F41.wireOp",EDGE,"E47.bottom")}),1.0]])]});
            extrude(context, id + "F42", {"entities" : qUnion([Q0]), "operationType" : NewBodyOperationType.REMOVE, "oppositeDirection" : true, "depth" : 736.6 * mm});
        }
        {
            var Q0;
            {var subQ0=sQuery(id+"F30.wireOp",EDGE,"E32.right");var subQ1=sQuery(id+"F30.wireOp",EDGE,"E32.top");var subQ2=makeQuery(id+"F30.imprint","INTERSECT",VERTEX,{"derivedFrom":[subQ1,subQ0]});Q0=makeQuery(id+"F30.imprint","IMPRINT",FACE,{"disambiguationData":[TD([[makeQuery(id+"F30.imprint","IMPRINT",EDGE,{"disambiguationData":[TD([[subQ2,1.0]])],"derivedFrom":subQ1}),-1.0]])]});}
            var Q1;
            {var subQ0=sQuery(id+"F30.wireOp",EDGE,"E32.right");var subQ1=sQuery(id+"F30.wireOp",EDGE,"E32.top");var subQ2=makeQuery(id+"F30.imprint","INTERSECT",VERTEX,{"derivedFrom":[subQ1,subQ0]});Q1=makeQuery(id+"F30.imprint","IMPRINT",FACE,{"disambiguationData":[TD([[makeQuery(id+"F30.imprint","IMPRINT",EDGE,{"disambiguationData":[TD([[subQ2,1.0]])],"derivedFrom":subQ1}),1.0]])]});}
            extrude(context, id + "F43", {"entities" : qUnion([Q0, Q1]), "operationType" : NewBodyOperationType.REMOVE, "oppositeDirection" : true, "depth" : 6.35 * mm});
        }
    });
